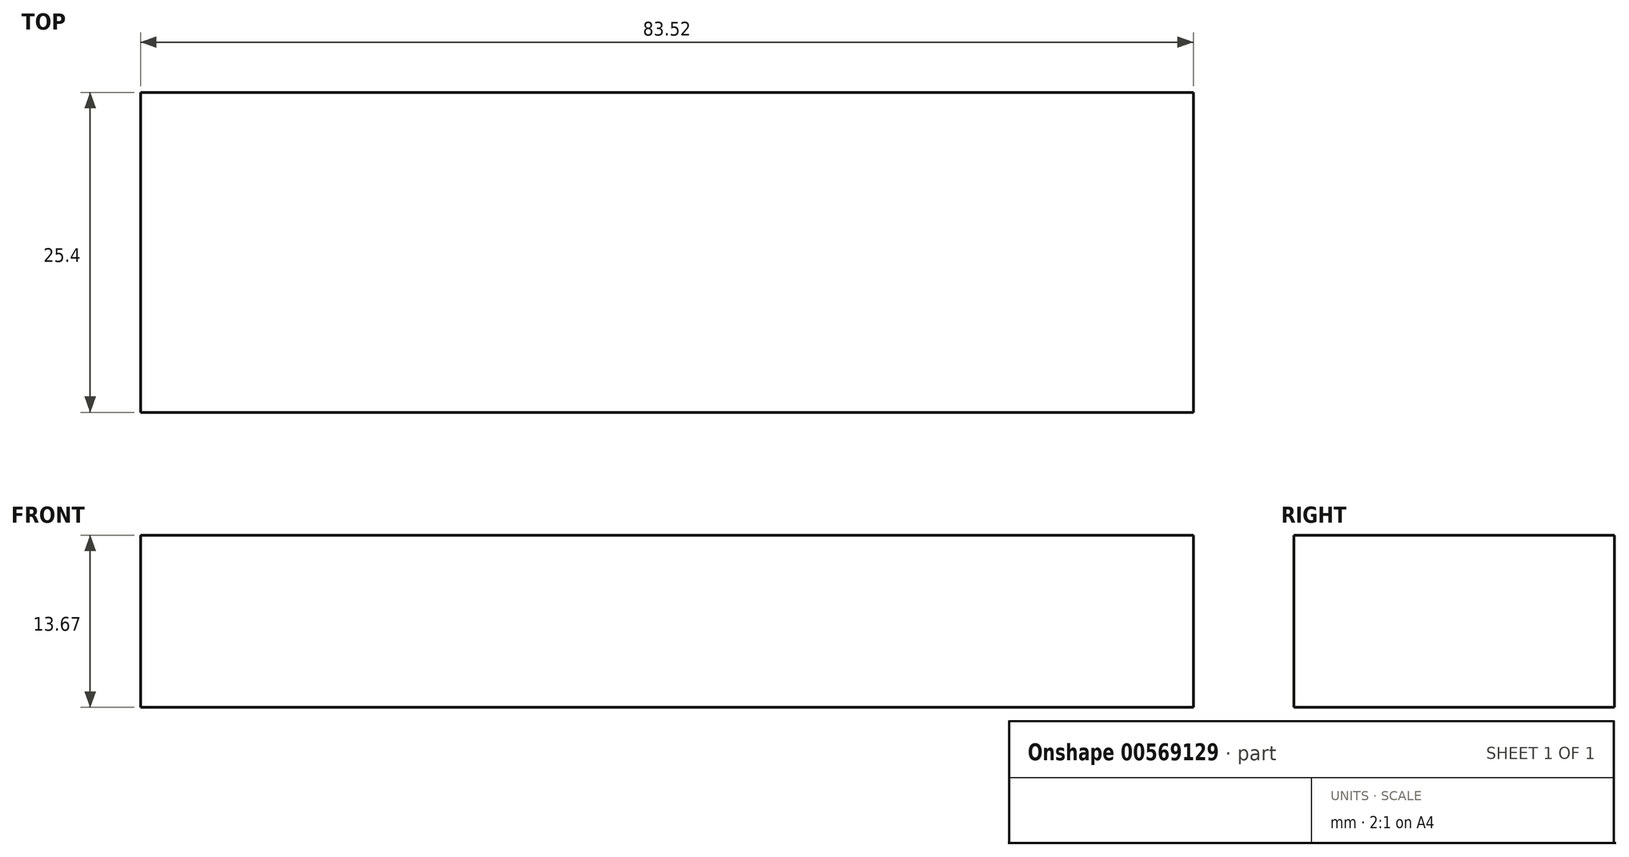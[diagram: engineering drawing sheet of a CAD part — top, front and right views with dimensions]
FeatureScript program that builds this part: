
annotation { "Feature Type Name" : "Feature", "Feature Type Description" : "" }
export const myFeature = defineFeature(function(context is Context, id is Id, definition is map)
    precondition{}
    {
        {
            var Q0;
            Q0=qCreatedBy(makeId("Front.planeOp"),FACE);
            var sketch = newSketch(context, id + "F0", { "sketchPlane" : qUnion([Q0])});
            skLineSegment(sketch, "E0.bottom", {"start": v(42.13, -42.5) * mm, "end": v(-41.39, -42.5) * mm});
            skLineSegment(sketch, "E0.top", {"start": v(42.13, -56.17) * mm, "end": v(-41.39, -56.17) * mm});
            skLineSegment(sketch, "E0.left", {"start": v(42.13, -42.5) * mm, "end": v(42.13, -56.17) * mm});
            skLineSegment(sketch, "E0.right", {"start": v(-41.39, -42.5) * mm, "end": v(-41.39, -56.17) * mm});
            skSolve(sketch);
        }
        {
            var Q0;
            Q0=makeQuery(id+"F0.imprint","IMPRINT",FACE,{"disambiguationData":[TD([[makeQuery(id+"F0.imprint","IMPRINT",EDGE,{"derivedFrom":sQuery(id+"F0.wireOp",EDGE,"E0.bottom")}),1.0]])]});
            extrude(context, id + "F1", {"entities" : qUnion([Q0]), "depth" : 25.4 * mm, "offsetDistance" : 25.4 * mm});
        }
    });
